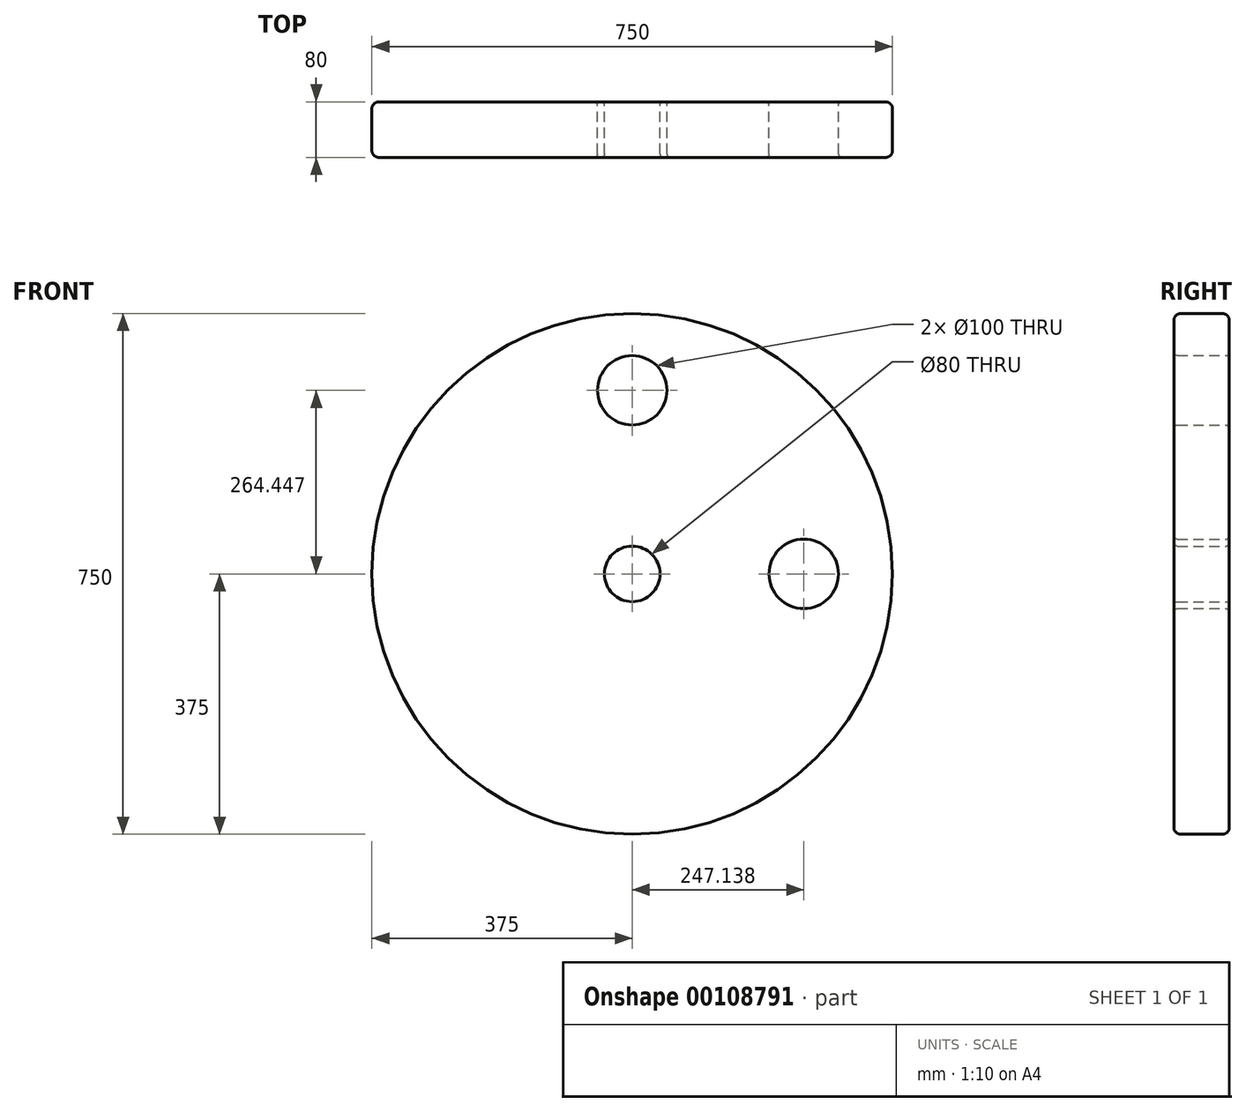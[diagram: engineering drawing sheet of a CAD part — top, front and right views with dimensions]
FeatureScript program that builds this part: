
annotation { "Feature Type Name" : "Feature", "Feature Type Description" : "" }
export const myFeature = defineFeature(function(context is Context, id is Id, definition is map)
    precondition{}
    {
        {
            var Q0;
            Q0=qCreatedBy(makeId("Front.planeOp"),FACE);
            var sketch = newSketch(context, id + "F0", { "sketchPlane" : qUnion([Q0])});
            skCircle(sketch, "E0", {"center": v(0, 0) * mm, "radius": 375 * mm});
            skLineSegment(sketch, "E1", {"start": v(0, 0) * mm, "end": v(0, 264.45) * mm});
            skLineSegment(sketch, "E2", {"start": v(0, 264.45) * mm, "end": v(0, 0) * mm});
            skLineSegment(sketch, "E3", {"start": v(0, 0) * mm, "end": v(247.14, 0) * mm});
            skCircle(sketch, "E4", {"center": v(247.14, 0) * mm, "radius": 50 * mm});
            skCircle(sketch, "E5", {"center": v(0, 264.45) * mm, "radius": 50 * mm});
            skCircle(sketch, "E6", {"center": v(0, 0) * mm, "radius": 40 * mm});
            skSolve(sketch);
        }
        {
            var Q0;
            Q0=makeQuery(id+"F0.imprint","IMPRINT",FACE,{"disambiguationData":[TD([[makeQuery(id+"F0.imprint","IMPRINT",EDGE,{"derivedFrom":sQuery(id+"F0.wireOp",EDGE,"E0")}),1.0]])]});
            var Q1;
            Q1=sQuery(id+"F0.wireOp",EDGE,"E0");
            extrude(context, id + "F1", {"entities" : qUnion([Q0]), "surfaceEntities" : qUnion([Q1]), "depth" : 80 * mm});
        }
        {
            var Q0;
            Q0=makeQuery(id+"F1.opExtrude","CAP_EDGE",EDGE,{"disambiguationData":[OSD([sQuery(id+"F0.wireOp",EDGE,"E5")])],"isStart":false});
            var Q1;
            Q1=makeQuery(id+"F1.opExtrude","CAP_EDGE",EDGE,{"disambiguationData":[OSD([sQuery(id+"F0.wireOp",EDGE,"E4")])],"isStart":false});
            var Q2;
            Q2=makeQuery(id+"F1.opExtrude","CAP_EDGE",EDGE,{"disambiguationData":[OSD([sQuery(id+"F0.wireOp",EDGE,"E6")])],"isStart":false});
            var Q3;
            Q3=makeQuery(id+"F1.opExtrude","CAP_EDGE",EDGE,{"disambiguationData":[OSD([sQuery(id+"F0.wireOp",EDGE,"E4")])],"isStart":true});
            var Q4;
            Q4=makeQuery(id+"F1.opExtrude","CAP_EDGE",EDGE,{"disambiguationData":[OSD([sQuery(id+"F0.wireOp",EDGE,"E6")])],"isStart":true});
            var Q5;
            Q5=makeQuery(id+"F1.opExtrude","CAP_EDGE",EDGE,{"disambiguationData":[OSD([sQuery(id+"F0.wireOp",EDGE,"E5")])],"isStart":true});
            fillet(context, id + "F2", {"entities" : qUnion([Q0, Q1, Q2, Q3, Q4, Q5]), "radius" : 5 * mm, "tangentPropagation" : true, "allowEdgeOverflow" : false});
        }
        {
            var Q0;
            Q0=makeQuery(id+"F1.opExtrude","CAP_EDGE",EDGE,{"disambiguationData":[OSD([sQuery(id+"F0.wireOp",EDGE,"E0")])],"isStart":true});
            var Q1;
            Q1=makeQuery(id+"F1.opExtrude","CAP_EDGE",EDGE,{"disambiguationData":[OSD([sQuery(id+"F0.wireOp",EDGE,"E0")])],"isStart":false});
            fillet(context, id + "F3", {"entities" : qUnion([Q0, Q1]), "radius" : 10 * mm, "tangentPropagation" : true, "allowEdgeOverflow" : false});
        }
    });
